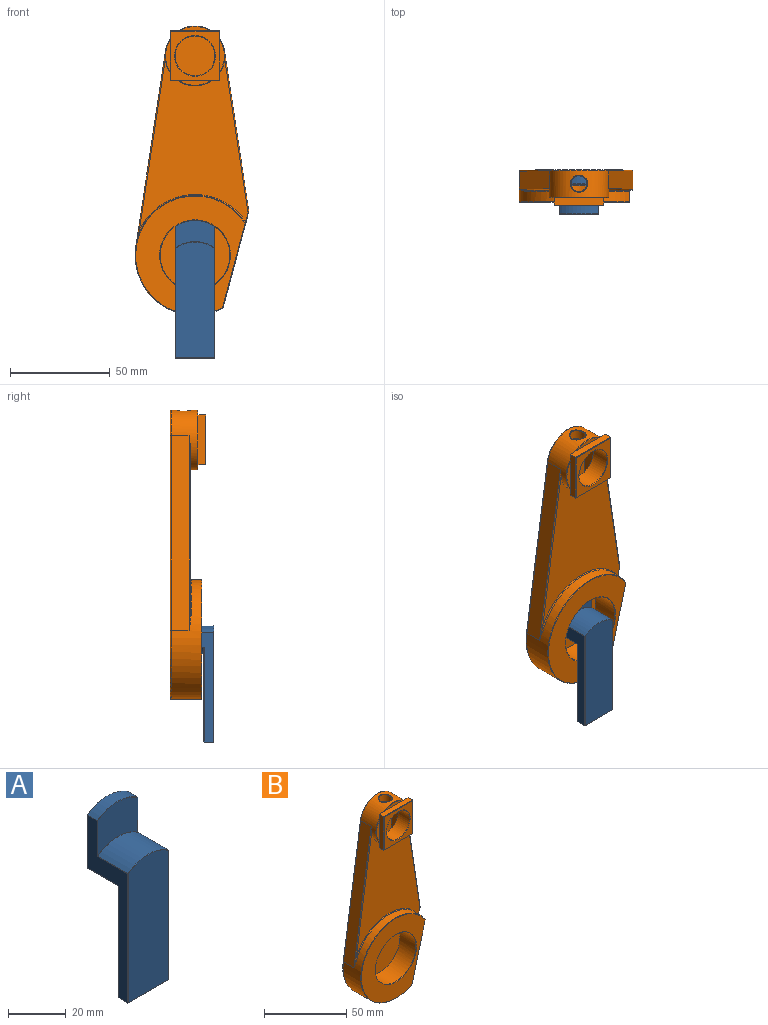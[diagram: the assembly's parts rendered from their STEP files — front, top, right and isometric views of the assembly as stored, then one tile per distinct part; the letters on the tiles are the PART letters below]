
ASSEMBLY  parts=2 mates=1
PART A: 38 faces, bbox 20x20x73.3 mm
  f0: plane 70x19.8mm, normal (-1,0,0), area 447mm2, adj f3,f7,f10,f11,f12,f15,f24,f25
  f1: cylinder r=17mm len=19.92mm, axis (0,-1,0), area 314.9mm2, adj f25,f32,f33,f37
  f2: plane 70x19.8mm, normal (1,0,0), area 447mm2, adj f3,f7,f17,f20,f22,f23,f31,f34
  f3: cylinder r=17mm len=20mm, axis (0,-1,0), area 102.6mm2, adj f0,f2,f16,f27
  f4: plane 28.8x19.8mm, normal (0,1,0), area 529.7mm2, adj f24,f27,f31,f32
  f5: plane 19.8x17.96mm, normal (0,-1,0), area 292.8mm2, adj f12,f16,f19,f20
  f6: cylinder r=17mm len=19.92mm, axis (0,1,0), area 314.9mm2, adj f11,f18,f19,f23
  f7: plane 20x4.8mm, normal (0,0,-1), area 96mm2, adj f0,f2,f13,f30
  f8: plane 58.05x19.8mm, normal (0,-1,0), area 1129.2mm2, adj f10,f13,f17,f18
  f9: plane 47.21x19.8mm, normal (0,1,0), area 892.2mm2, adj f26,f30,f33,f34
  f10: plane 54.95x0.1mm, normal (-0.71,-0.71,0), area 7.8mm2, adj f0,f8,f13,f14
  f11: plane 14.8x0.08mm, normal (-0.89,0,0.46), area 1.3mm2, adj f0,f6,f14,f15
  f12: plane 14.81x0.1mm, normal (-0.71,-0.71,0), area 2.1mm2, adj f0,f5,f15,f16
  f13: plane 20x0.1mm, normal (0,-0.71,-0.71), area 2.8mm2, adj f7,f8,f10,f17
  f14: plane 0.1x0.1mm, normal (-0.67,-0.67,0.34), area 0mm2, adj f10,f11,f18
  f15: bspline ~0.25x0.2mm, area 0mm2, adj f0,f11,f12,f19
  f16: cone r=16.9mm half-angle=45deg, axis (0,1,0), area 3mm2, adj f3,f5,f12,f20
  f17: plane 54.95x0.1mm, normal (0.71,-0.71,0), area 7.8mm2, adj f2,f8,f13,f21
  f18: cone r=16.9mm half-angle=45deg, axis (0,1,0), area 3mm2, adj f6,f8,f14,f21
  f19: cone r=17mm half-angle=45deg, axis (0,1,0), area 3mm2, adj f5,f6,f15,f22
  f20: plane 14.81x0.1mm, normal (0.71,-0.71,0), area 2.1mm2, adj f2,f5,f16,f22
  f21: plane 0.1x0.1mm, normal (0.67,-0.67,0.34), area 0mm2, adj f17,f18,f23
  f22: bspline ~0.25x0.2mm, area 0mm2, adj f2,f19,f20,f23
  f23: plane 14.8x0.08mm, normal (0.89,0,0.46), area 1.3mm2, adj f2,f6,f21,f22
  f24: plane 22.44x0.1mm, normal (-0.71,0.71,0), area 3.2mm2, adj f0,f4,f27,f28
  f25: plane 14.8x0.08mm, normal (-0.89,0,-0.46), area 1.3mm2, adj f0,f1,f28,f29
  f26: plane 47.31x0.1mm, normal (-0.71,0.71,0), area 6.7mm2, adj f0,f9,f29,f30
  f27: cone r=17mm half-angle=45deg, axis (0,-1,0), area 3mm2, adj f3,f4,f24,f31
  f28: plane 0.1x0.1mm, normal (-0.67,0.67,-0.34), area 0mm2, adj f24,f25,f32
  f29: bspline ~0.25x0.2mm, area 0mm2, adj f0,f25,f26,f33
  f30: plane 20x0.1mm, normal (0,0.71,-0.71), area 2.8mm2, adj f7,f9,f26,f34
  f31: plane 22.44x0.1mm, normal (0.71,0.71,0), area 3.2mm2, adj f2,f4,f27,f35
  f32: cone r=17mm half-angle=45deg, axis (0,-1,0), area 3mm2, adj f1,f4,f28,f35
  f33: cone r=17.1mm half-angle=45deg, axis (0,-1,0), area 3mm2, adj f1,f9,f29,f36
  f34: plane 47.31x0.1mm, normal (0.71,0.71,0), area 6.7mm2, adj f2,f9,f30,f36
  f35: plane 0.1x0.1mm, normal (0.67,0.67,-0.34), area 0mm2, adj f31,f32,f37
  f36: bspline ~0.25x0.2mm, area 0mm2, adj f2,f33,f34,f37
  f37: plane 14.8x0.08mm, normal (0.89,0,-0.46), area 1.3mm2, adj f1,f2,f35,f36
PART B: 62 faces, bbox 60.7x18x148.7 mm
  f0: plane 15.66x2.25mm, normal (0,-1,0), area 23.9mm2, adj f15,f52
  f1: plane 15.66x2.25mm, normal (0,-1,0), area 23.9mm2, adj f18,f51
  f2: plane 15.66x2.25mm, normal (0,-1,0), area 23.9mm2, adj f17,f54
  f3: cylinder r=15mm len=30mm, axis (0,-1,0), area 708.2mm2, adj f4,f7,f9,f11,f12,f13,f14,f15
  f4: plane 97.75x14.83mm, normal (-0.99,0,0.15), area 889.8mm2, adj f3,f5,f32,f34
  f5: cylinder r=30mm len=60mm, axis (0,-1,0), area 1393.9mm2, adj f4,f30,f35,f36,f41,f43,f46
  f6: plane 48.34x15.52mm, normal (0.97,0,-0.26), area 738.2mm2, adj f29,f38,f39,f40,f41,f44,f46,f47
  f7: plane 80.14x12.16mm, normal (0.99,0,0.15), area 729.5mm2, adj f3,f28,f29,f31
  f8: plane 144x56.09mm, normal (0,1,0), area 5852.1mm2, adj f30,f31,f32,f33,f48
  f9: plane 86.29x54.59mm, normal (0,-1,0), area 2646.3mm2, adj f3,f28,f34,f36,f39
  f10: plane 15.66x2.25mm, normal (0,-1,0), area 23.9mm2, adj f16,f53
  f11: plane 4.21x4.21mm, normal (0,1,0), area 7.7mm2, adj f3,f15,f16
  f12: plane 4.21x4.21mm, normal (0,1,0), area 7.7mm2, adj f3,f16,f17
  f13: plane 4.21x4.21mm, normal (0,1,0), area 7.7mm2, adj f3,f17,f18
  f14: plane 4.21x4.21mm, normal (0,1,0), area 7.7mm2, adj f3,f15,f18
  f15: plane 25x4mm, normal (0,0,-1), area 93.9mm2, adj f0,f3,f11,f14,f16,f18,f52,f59
  f16: plane 25x4mm, normal (1,0,0), area 93.9mm2, adj f3,f10,f11,f12,f15,f17,f53,f57
  f17: plane 25x4mm, normal (0,0,1), area 93.9mm2, adj f2,f3,f12,f13,f16,f18,f54,f56
  f18: plane 25x4mm, normal (-1,0,0), area 93.9mm2, adj f1,f3,f13,f14,f15,f17,f51,f58
  f19: plane 24.5x24.5mm, normal (0,-1,0), area 270.2mm2, adj f55,f56,f57,f58,f59
  f20: cylinder r=10mm len=20mm, axis (0,1,0), area 749.8mm2, adj f23,f24,f25,f26,f27,f55
  f21: cylinder r=17.5mm len=35mm, axis (0,1,0), area 1384.2mm2, adj f23,f24,f25,f26,f61
  f22: plane 59.5x54.87mm, normal (0,-1,0), area 1499.6mm2, adj f43,f44,f61
  f23: plane 127.5x35mm, normal (0,-1,0), area 2789.3mm2, adj f20,f21,f24,f26
  f24: plane 85.64x6mm, normal (1,0,0), area 513.8mm2, adj f20,f21,f23,f25
  f25: plane 85.64x20mm, normal (0,1,0), area 1513mm2, adj f20,f21,f24,f26
  f26: plane 85.64x6mm, normal (-1,0,0), area 513.8mm2, adj f20,f21,f23,f25
  f27: cylinder r=4mm len=8mm, axis (0,0,1), area 124.6mm2, adj f20,f60
  f28: cylinder r=0.5mm len=80.84mm, axis (-0.15,0,0.99), area 62.4mm2, adj f3,f7,f9,f37,f38
  f29: cylinder r=0.5mm len=9.2mm, axis (0,-1,0), area 1.9mm2, adj f6,f7,f37,f50
  f30: torus R=29.5mm, axis (0,-1,0), area 51.7mm2, adj f5,f8,f32,f47
  f31: cylinder r=0.5mm len=80.84mm, axis (0.15,0,-0.99), area 63.9mm2, adj f7,f8,f33,f49,f50
  f32: cylinder r=0.5mm len=97.83mm, axis (0.15,0,0.99), area 77.7mm2, adj f4,f8,f30,f33
  f33: torus R=14.5mm, axis (0,-1,0), area 33.1mm2, adj f3,f8,f31,f32
  f34: cylinder r=0.5mm len=97.83mm, axis (-0.15,0,-0.99), area 73.1mm2, adj f3,f4,f9,f35
  f35: bspline ~8.21x2.38mm, area 2mm2, adj f5,f34,f36
  f36: torus R=30.5mm, axis (0,-1,0), area 51.1mm2, adj f5,f9,f35,f40
  f37: bspline ~0.2x0.2mm, area 0mm2, adj f28,f29,f38
  f38: bspline ~0.65x0.4mm, area 0.2mm2, adj f6,f28,f37,f39
  f39: plane 4.57x1.45mm, normal (0.68,-0.71,-0.18), area 1.6mm2, adj f6,f9,f38,f40
  f40: bspline ~1.04x0.75mm, area 0.3mm2, adj f6,f36,f39,f41
  f41: plane 5.25x0.2mm, normal (0.99,0,0.15), area 1.1mm2, adj f5,f6,f40,f42
  f42: plane 0.25x0.24mm, normal (0.73,-0.68,0.11), area 0mm2, adj f41,f43,f44
  f43: cone r=29.75mm half-angle=45deg, axis (0,1,0), area 48.9mm2, adj f5,f22,f42,f45
  f44: plane 42.36x11.58mm, normal (0.68,-0.71,-0.18), area 15.5mm2, adj f6,f22,f42,f45
  f45: plane 0.25x0.24mm, normal (0.58,-0.68,-0.46), area 0mm2, adj f43,f44,f46
  f46: plane 15.25x0.16mm, normal (0.78,0,-0.63), area 3.1mm2, adj f5,f6,f45,f47
  f47: bspline ~0.55x0.51mm, area 0.2mm2, adj f6,f30,f46,f48
  f48: plane 47.51x12.96mm, normal (0.68,0.71,-0.18), area 17.4mm2, adj f6,f8,f47,f49
  f49: bspline ~0.65x0.4mm, area 0.2mm2, adj f6,f31,f48,f50
  f50: bspline ~0.2x0.2mm, area 0mm2, adj f29,f31,f49
  f51: cone r=14.75mm half-angle=45deg, axis (0,1,0), area 6mm2, adj f1,f3,f18
  f52: cone r=14.75mm half-angle=45deg, axis (0,1,0), area 6mm2, adj f0,f3,f15
  f53: cone r=14.75mm half-angle=45deg, axis (0,1,0), area 6mm2, adj f3,f10,f16
  f54: cone r=14.75mm half-angle=45deg, axis (0,1,0), area 6mm2, adj f2,f3,f17
  f55: cone r=10mm half-angle=45deg, axis (0,-1,0), area 22.5mm2, adj f19,f20
  f56: plane 25x0.25mm, normal (0,-0.71,0.71), area 8.8mm2, adj f17,f19,f57,f58
  f57: plane 25x0.25mm, normal (0.71,-0.71,0), area 8.8mm2, adj f16,f19,f56,f59
  f58: plane 25x0.25mm, normal (-0.71,-0.71,0), area 8.8mm2, adj f18,f19,f56,f59
  f59: plane 25x0.25mm, normal (0,-0.71,-0.71), area 8.8mm2, adj f15,f19,f57,f58
  f60: bspline ~8.64x8.5mm, area 9.9mm2, adj f3,f27
  f61: cone r=17.5mm half-angle=45deg, axis (0,-1,0), area 39.2mm2, adj f21,f22
PLACE A at identity fixed
PLACE B t=(0,-3,61.5)mm
MATE parallel B.f21 <-> A.f4  axis (0,1,0) through (0,5,16.5)mm
